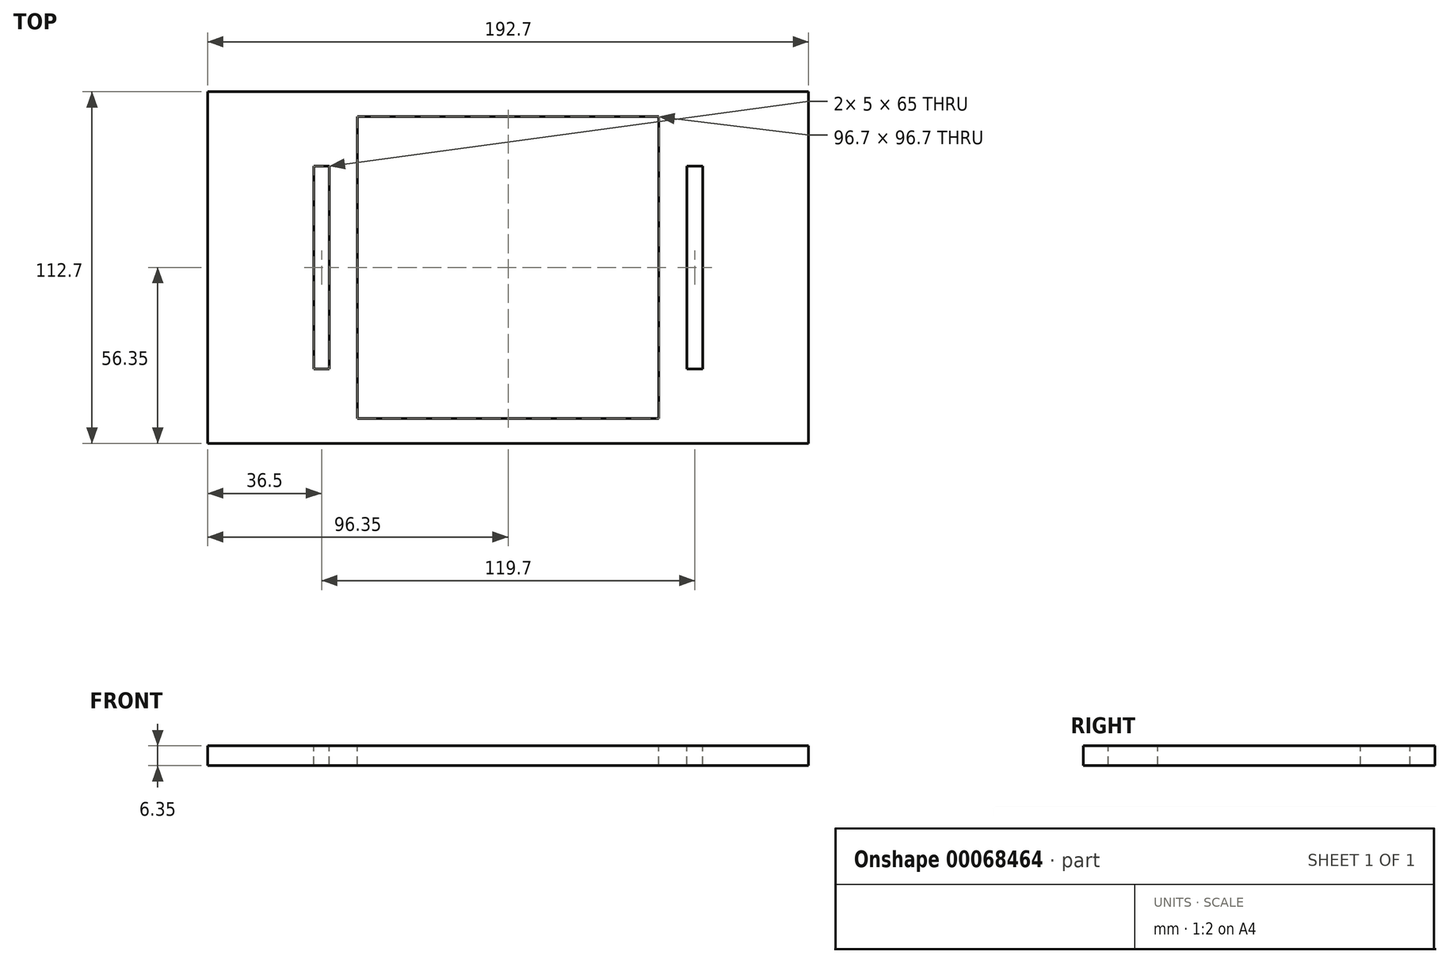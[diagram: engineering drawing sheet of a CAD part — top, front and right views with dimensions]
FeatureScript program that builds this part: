
annotation { "Feature Type Name" : "Feature", "Feature Type Description" : "" }
export const myFeature = defineFeature(function(context is Context, id is Id, definition is map)
    precondition{}
    {
        {
            var Q0;
            Q0=qCreatedBy(makeId("Top.planeOp"),FACE);
            var sketch = newSketch(context, id + "F0", { "sketchPlane" : qUnion([Q0])});
            skLineSegment(sketch, "E0.rect.bottom", {"start": v(96.35, 56.35) * mm, "end": v(-96.35, 56.35) * mm});
            skLineSegment(sketch, "E0.rect.top", {"start": v(96.35, -56.35) * mm, "end": v(-96.35, -56.35) * mm});
            skLineSegment(sketch, "E0.rect.left", {"start": v(96.35, 56.35) * mm, "end": v(96.35, -56.35) * mm});
            skLineSegment(sketch, "E0.rect.right", {"start": v(-96.35, 56.35) * mm, "end": v(-96.35, -56.35) * mm});
            skPoint(sketch, "E0.rect.middle", {"position": v(0, 0) * mm});
            skSolve(sketch);
        }
        {
            var Q0;
            Q0=makeQuery(id+"F0.imprint","IMPRINT",FACE,{"disambiguationData":[TD([[makeQuery(id+"F0.imprint","IMPRINT",EDGE,{"derivedFrom":sQuery(id+"F0.wireOp",EDGE,"E0.rect.bottom")}),1.0]])]});
            extrude(context, id + "F1", {"entities" : qUnion([Q0]), "depth" : 6.35 * mm});
        }
        {
            var Q0;
            Q0=makeQuery(id+"F1.opExtrude","CAP_FACE",FACE,{"disambiguationData":[OSD([sQuery(id+"F0.wireOp",EDGE,"E0.rect.bottom"),sQuery(id+"F0.wireOp",EDGE,"E0.rect.top"),sQuery(id+"F0.wireOp",EDGE,"E0.rect.left"),sQuery(id+"F0.wireOp",EDGE,"E0.rect.right")])],"isStart":false});
            var sketch = newSketch(context, id + "F2", { "sketchPlane" : qUnion([Q0])});
            skLineSegment(sketch, "E1.rect.bottom", {"start": v(48.35, 48.35) * mm, "end": v(-48.35, 48.35) * mm});
            skLineSegment(sketch, "E1.rect.top", {"start": v(48.35, -48.35) * mm, "end": v(-48.35, -48.35) * mm});
            skLineSegment(sketch, "E1.rect.left", {"start": v(48.35, 48.35) * mm, "end": v(48.35, -48.35) * mm});
            skLineSegment(sketch, "E1.rect.right", {"start": v(-48.35, 48.35) * mm, "end": v(-48.35, -48.35) * mm});
            skPoint(sketch, "E1.rect.middle", {"position": v(0, 0) * mm});
            skLineSegment(sketch, "E2.bottom", {"start": v(57.35, 32.5) * mm, "end": v(62.35, 32.5) * mm});
            skLineSegment(sketch, "E2.top", {"start": v(57.35, -32.5) * mm, "end": v(62.35, -32.5) * mm});
            skLineSegment(sketch, "E2.left", {"start": v(57.35, 32.5) * mm, "end": v(57.35, -32.5) * mm});
            skLineSegment(sketch, "E2.right", {"start": v(62.35, 32.5) * mm, "end": v(62.35, -32.5) * mm});
            skLineSegment(sketch, "E3", {"start": v(57.35, 32.5) * mm, "end": v(57.35, 56.35) * mm, "construction": true});
            skLineSegment(sketch, "E4", {"start": v(57.35, -32.5) * mm, "end": v(57.35, -56.35) * mm, "construction": true});
            skLineSegment(sketch, "E5", {"start": v(62.35, 32.5) * mm, "end": v(96.35, 32.5) * mm, "construction": true});
            skLineSegment(sketch, "E6.MirrorCS", {"start": v(-62.35, 32.5) * mm, "end": v(-62.35, -32.5) * mm});
            skLineSegment(sketch, "E7.MirrorCS", {"start": v(-57.35, -32.5) * mm, "end": v(-62.35, -32.5) * mm});
            skLineSegment(sketch, "E8.MirrorCS", {"start": v(-57.35, 32.5) * mm, "end": v(-62.35, 32.5) * mm});
            skLineSegment(sketch, "E9.MirrorCS", {"start": v(-57.35, 32.5) * mm, "end": v(-57.35, -32.5) * mm});
            skLineSegment(sketch, "E10.MirrorCS", {"start": v(-62.35, 32.5) * mm, "end": v(-96.35, 32.5) * mm, "construction": true});
            skLineSegment(sketch, "E11.MirrorCS", {"start": v(-57.35, -32.5) * mm, "end": v(-57.35, -56.35) * mm, "construction": true});
            skLineSegment(sketch, "E12.MirrorCS", {"start": v(-57.35, 32.5) * mm, "end": v(-57.35, 56.35) * mm, "construction": true});
            skSolve(sketch);
        }
        {
            var Q0;
            Q0=makeQuery(id+"F2.imprint","IMPRINT",FACE,{"disambiguationData":[TD([[makeQuery(id+"F2.imprint","IMPRINT",EDGE,{"derivedFrom":sQuery(id+"F2.wireOp",EDGE,"E1.rect.bottom")}),1.0]])]});
            var Q1;
            Q1=makeQuery(id+"F2.imprint","IMPRINT",FACE,{"disambiguationData":[TD([[makeQuery(id+"F2.imprint","IMPRINT",EDGE,{"derivedFrom":sQuery(id+"F2.wireOp",EDGE,"E6.MirrorCS")}),1.0]])]});
            var Q2;
            Q2=makeQuery(id+"F2.imprint","IMPRINT",FACE,{"disambiguationData":[TD([[makeQuery(id+"F2.imprint","IMPRINT",EDGE,{"derivedFrom":sQuery(id+"F2.wireOp",EDGE,"E2.bottom")}),-1.0]])]});
            extrude(context, id + "F3", {"entities" : qUnion([Q0, Q1, Q2]), "operationType" : NewBodyOperationType.REMOVE, "endBound" : BoundingType.THROUGH_ALL, "oppositeDirection" : true, "depth" : 25 * mm});
        }
    });
